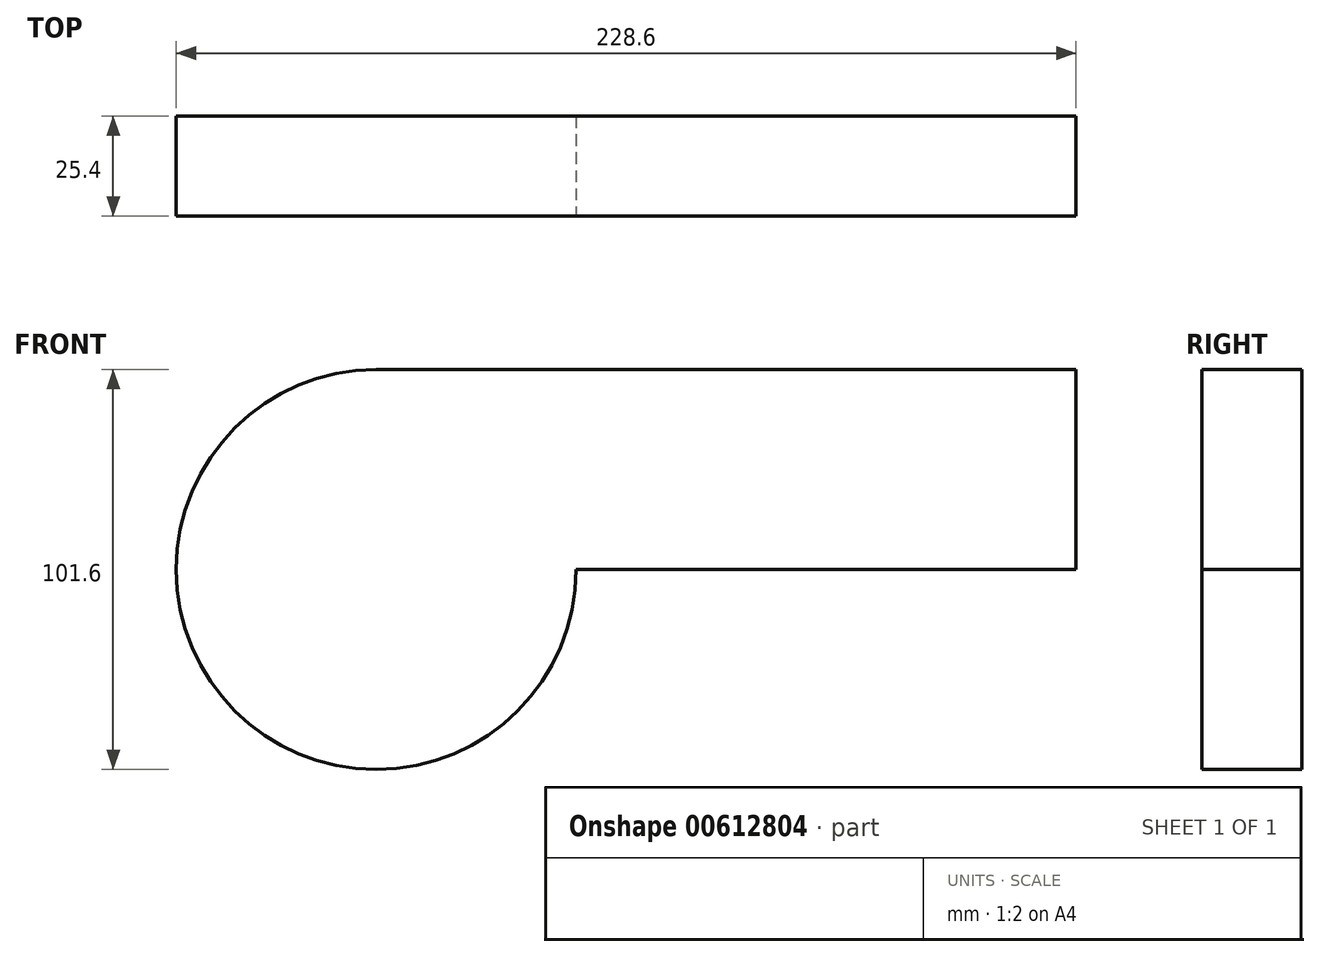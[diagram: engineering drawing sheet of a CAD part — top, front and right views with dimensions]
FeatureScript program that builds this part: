
annotation { "Feature Type Name" : "Feature", "Feature Type Description" : "" }
export const myFeature = defineFeature(function(context is Context, id is Id, definition is map)
    precondition{}
    {
        {
            var Q0;
            Q0=qCreatedBy(makeId("Front.planeOp"),FACE);
            var sketch = newSketch(context, id + "F0", { "sketchPlane" : qUnion([Q0])});
            skLineSegment(sketch, "E0", {"start": v(-105.98, -25.98) * mm, "end": v(105.51, -25.98) * mm});
            skLineSegment(sketch, "E1.bottom", {"start": v(-105.98, -25.98) * mm, "end": v(71.82, -25.98) * mm});
            skLineSegment(sketch, "E1.top", {"start": v(-105.98, -76.78) * mm, "end": v(71.82, -76.78) * mm});
            skLineSegment(sketch, "E1.left", {"start": v(-105.98, -25.98) * mm, "end": v(-105.98, -76.78) * mm});
            skLineSegment(sketch, "E1.right", {"start": v(71.82, -25.98) * mm, "end": v(71.82, -76.78) * mm});
            skSolve(sketch);
        }
        {
            var Q0;
            Q0=makeQuery(id+"F0.imprint","IMPRINT",FACE,{"disambiguationData":[TD([[makeQuery(id+"F0.imprint","IMPRINT",EDGE,{"derivedFrom":sQuery(id+"F0.wireOp",EDGE,"E1.top")}),1.0]])]});
            extrude(context, id + "F1", {"entities" : qUnion([Q0]), "depth" : 25.4 * mm, "offsetDistance" : 25.4 * mm});
        }
        {
            var Q0;
            Q0=makeQuery(id+"F1.opExtrude","SWEPT_FACE",FACE,{"disambiguationData":[OSD([sQuery(id+"F0.wireOp",EDGE,"E1.left")])]});
            var Q1;
            Q1=makeQuery(id+"F1.opExtrude","SWEPT_EDGE",EDGE,{"disambiguationData":[OSD([sQuery(id+"F0.wireOp",EDGE,"E1.top"),sQuery(id+"F0.wireOp",EDGE,"E1.left")])]});
            revolve(context, id + "F2", {"operationType" : NewBodyOperationType.ADD, "entities" : qUnion([Q0]), "axis" : qUnion([Q1]), "revolveType" : RevolveType.FULL});
        }
    });
